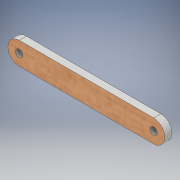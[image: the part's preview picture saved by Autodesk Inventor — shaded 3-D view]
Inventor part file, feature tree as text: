
AUTODESK INVENTOR PART (.ipt)
format: ipt  version: 2018 (Build 220112000, 112)  size: 113,152 bytes
history: native  units: mm
features: extrude x1, sketch x1
ambient origin geometry x8: Origin, YZ Plane, XZ Plane, XY Plane, X Axis, Y Axis, Z Axis, Center Point
bodies: Solid1 (feature_tree)
feature tree (2):
  extrude  "Extrusion1"  Depth=3.2mm
  sketch  "Sketch1"  dims[d0=3.2mm d1=3.2mm d2=59.755753mm d5=3.2mm d6=0.0mm d12=10.0mm d13=10.0mm]
